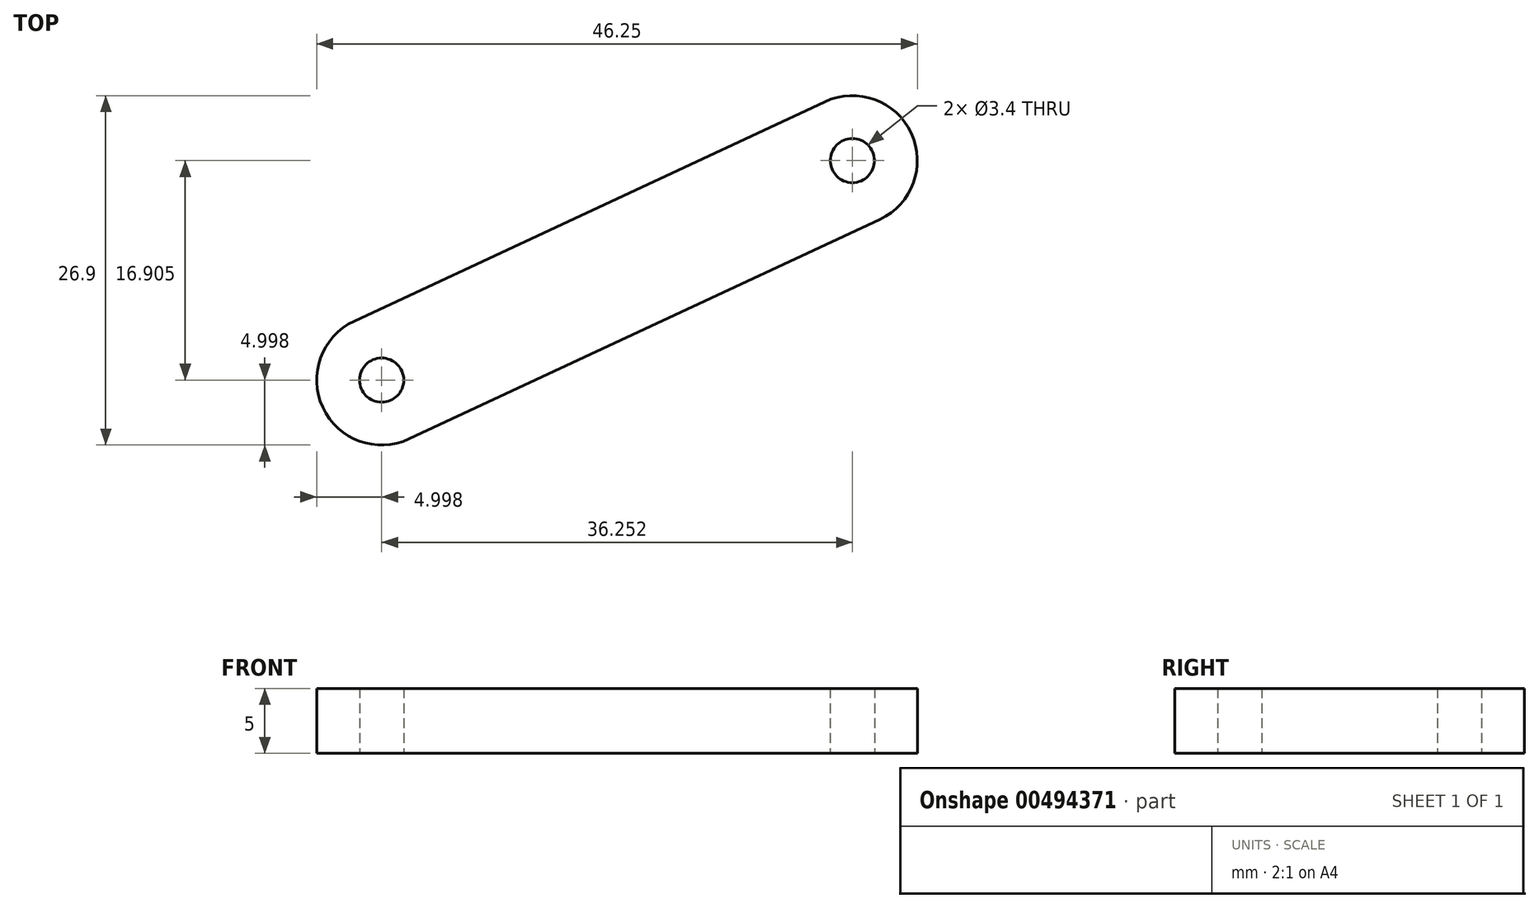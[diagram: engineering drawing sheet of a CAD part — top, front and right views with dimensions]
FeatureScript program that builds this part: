
annotation { "Feature Type Name" : "Feature", "Feature Type Description" : "" }
export const myFeature = defineFeature(function(context is Context, id is Id, definition is map)
    precondition{}
    {
        {
            var Q0;
            Q0=qCreatedBy(makeId("Top.planeOp"),FACE);
            var sketch = newSketch(context, id + "F0", { "sketchPlane" : qUnion([Q0])});
            skLineSegment(sketch, "E0.left", {"start": v(-5, 17.14) * mm, "end": v(-5, -22.86) * mm});
            skLineSegment(sketch, "E0.right", {"start": v(5, 17.14) * mm, "end": v(5, -22.86) * mm});
            skArc(sketch, "E1", {"start": v(-5, 17.14) * mm, "mid": v(0, 22.14) * mm, "end": v(5, 17.14) * mm});
            skArc(sketch, "E2", {"start": v(-5, -22.86) * mm, "mid": v(0, -27.86) * mm, "end": v(5, -22.86) * mm});
            skCircle(sketch, "E3", {"center": v(0, -22.86) * mm, "radius": 1.7 * mm});
            skCircle(sketch, "E4", {"center": v(0, 17.14) * mm, "radius": 1.7 * mm});
            skSolve(sketch);
        }
        {
            var Q0;
            Q0 = qSketchRegion(id + "F0", true);
            extrude(context, id + "F1", {"entities" : qUnion([Q0]), "depth" : 5 * mm});
        }
        {
            var Q0;
            Q0=makeQuery(id+"F1.opExtrude","SWEPT_BODY",BODY,{"disambiguationData":[OSD([sQuery(id+"F0.wireOp",EDGE,"E0.left"),sQuery(id+"F0.wireOp",EDGE,"E0.right"),sQuery(id+"F0.wireOp",EDGE,"E1"),sQuery(id+"F0.wireOp",EDGE,"E2"),sQuery(id+"F0.wireOp",EDGE,"E3"),sQuery(id+"F0.wireOp",EDGE,"E4")])]});
            var Q1;
            Q1=makeQuery(id+"F1.opExtrude","CAP_EDGE",EDGE,{"disambiguationData":[OSD([sQuery(id+"F0.wireOp",EDGE,"E4")])],"isStart":false});
            transform(context, id + "F2", {"entities" : qUnion([Q0]), "transformType" : TransformType.ROTATION, "transformAxis" : qUnion([Q1]), "angle" : 65 * degree, "oppositeDirection" : true, "makeCopy" : false});
        }
    });
